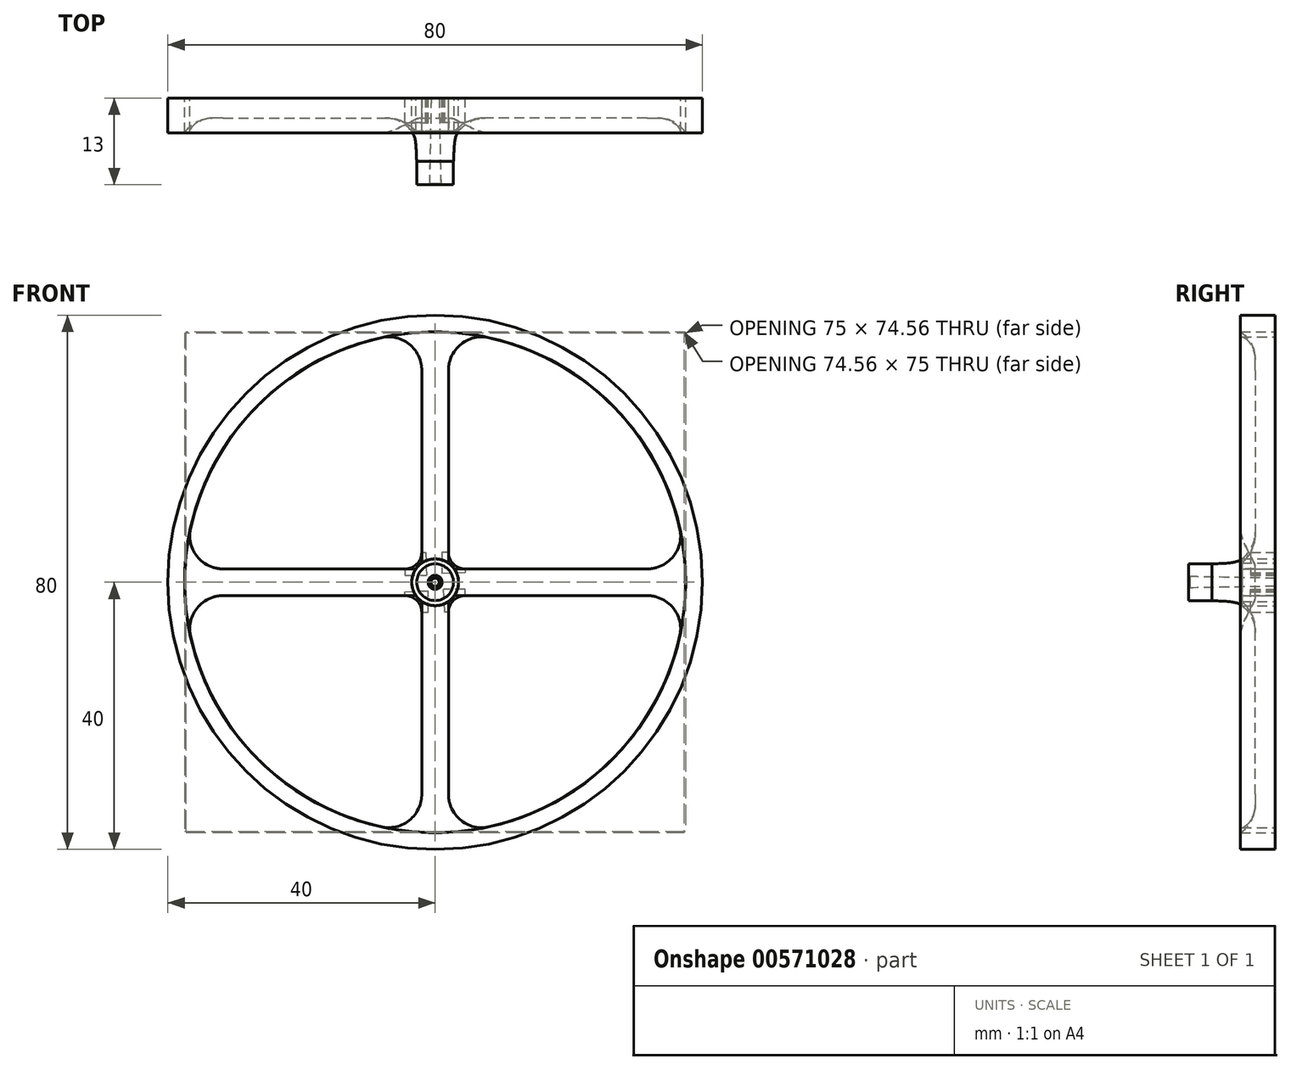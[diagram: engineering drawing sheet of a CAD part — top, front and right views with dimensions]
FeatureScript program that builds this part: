
annotation { "Feature Type Name" : "Feature", "Feature Type Description" : "" }
export const myFeature = defineFeature(function(context is Context, id is Id, definition is map)
    precondition{}
    {
        {
            var Q0;
            Q0=qCreatedBy(makeId("Front.planeOp"),FACE);
            var sketch = newSketch(context, id + "F0", { "sketchPlane" : qUnion([Q0])});
            skCircle(sketch, "E0", {"center": v(0, 0) * mm, "radius": 3.5 * mm});
            skSolve(sketch);
        }
        {
            var Q0;
            Q0=qSketchRegion(id+"F0",true);
            extrude(context, id + "F1", {"entities" : qUnion([Q0]), "depth" : 5 * mm});
        }
        {
            var Q0;
            Q0=qCreatedBy(makeId("Right.planeOp"),FACE);
            var sketch = newSketch(context, id + "F2", { "sketchPlane" : qUnion([Q0])});
            skLineSegment(sketch, "E1", {"start": v(3.77, 0) * mm, "end": v(-36.31, 0) * mm, "construction": true});
            skLineSegment(sketch, "E2", {"start": v(-13, 0) * mm, "end": v(-13, 2.75) * mm});
            skLineSegment(sketch, "E3", {"start": v(-13, 2.75) * mm, "end": v(-9.5, 2.75) * mm});
            skFitSpline(sketch, "E4", {"points": [v(-9.5, 2.75) * mm, v(-5, 3.5) * mm], "startDerivative": vector(5.34, 0.31) * mm, "endDerivative": vector(2.38, 2.14) * mm});
            skLineSegment(sketch, "E5", {"start": v(-5, 3.5) * mm, "end": v(-5, 0) * mm});
            skLineSegment(sketch, "E6", {"start": v(-5, 0) * mm, "end": v(-13, 0) * mm});
            skSolve(sketch);
        }
        {
            var Q0;
            Q0=qSketchRegion(id+"F2",true);
            var Q1;
            Q1=sQuery(id+"F2.wireOp",EDGE,"E1");
            revolve(context, id + "F3", {"operationType" : NewBodyOperationType.ADD, "entities" : qUnion([Q0]), "axis" : qUnion([Q1]), "revolveType" : RevolveType.FULL});
        }
        {
            var Q0;
            Q0=makeQuery(id+"F1.opExtrude","CAP_FACE",FACE,{"disambiguationData":[OSD([sQuery(id+"F0.wireOp",EDGE,"E0")])],"isStart":true});
            var sketch = newSketch(context, id + "F4", { "sketchPlane" : qUnion([Q0])});
            skCircle(sketch, "E7", {"center": v(0, 0) * mm, "radius": 0.6 * mm});
            skSolve(sketch);
        }
        {
            var Q0;
            Q0=qSketchRegion(id+"F4",true);
            extrude(context, id + "F5", {"entities" : qUnion([Q0]), "operationType" : NewBodyOperationType.REMOVE, "endBound" : BoundingType.THROUGH_ALL, "oppositeDirection" : true, "depth" : 25 * mm, "hasDraft" : true, "draftAngle" : 1.1 * degree});
        }
        {
            var Q0;
            Q0=qCreatedBy(makeId("Top.planeOp"),FACE);
            var sketch = newSketch(context, id + "F6", { "sketchPlane" : qUnion([Q0])});
            skLineSegment(sketch, "E8.bottom", {"start": v(-2, 0) * mm, "end": v(2, 0) * mm});
            skLineSegment(sketch, "E8.top", {"start": v(-2, -3) * mm, "end": v(2, -3) * mm});
            skLineSegment(sketch, "E8.left", {"start": v(-2, 0) * mm, "end": v(-2, -3) * mm});
            skLineSegment(sketch, "E8.right", {"start": v(2, 0) * mm, "end": v(2, -3) * mm});
            skSolve(sketch);
        }
        {
            var Q0;
            Q0=qSketchRegion(id+"F6",true);
            extrude(context, id + "F7", {"entities" : qUnion([Q0]), "operationType" : NewBodyOperationType.ADD, "depth" : 38 * mm, "hasSecondDirection" : true, "secondDirectionOppositeDirection" : false, "secondDirectionDepth" : 2.5 * mm, "offsetDistance" : 25 * mm});
        }
        {
            var Q0;
            Q0=makeQuery(id+"F5.boolean.opBoolean","INTERSECT",EDGE,{"derivedFrom":[makeQuery(id+"F3.opRevolve","SWEPT_FACE",FACE,{"disambiguationData":[OSD([sQuery(id+"F2.wireOp",EDGE,"E2")])]}),makeQuery(id+"F5.opExtrude","SWEPT_FACE",FACE,{"disambiguationData":[OSD([sQuery(id+"F4.wireOp",EDGE,"E7")])]})]});
            chamfer(context, id + "F8", {"entities" : qUnion([Q0]), "width" : .2 * mm, "tangentPropagation" : true});
        }
        {
            var Q0;
            Q0=makeQuery(id+"F7.boolean.opBoolean","MERGE",FACE,{"derivedFrom":[makeQuery(id+"F1.opExtrude","CAP_FACE",FACE,{"disambiguationData":[OSD([sQuery(id+"F0.wireOp",EDGE,"E0")])],"isStart":true}),makeQuery(id+"F7.opExtrude","SWEPT_FACE",FACE,{"disambiguationData":[OSD([sQuery(id+"F6.wireOp",EDGE,"E8.bottom")])]})]});
            var sketch = newSketch(context, id + "F9", { "sketchPlane" : qUnion([Q0])});
            skCircle(sketch, "E9", {"center": v(0, 0) * mm, "radius": 40 * mm});
            skCircle(sketch, "E10", {"center": v(0, 0) * mm, "radius": 37.5 * mm});
            skSolve(sketch);
        }
        {
            var Q0;
            Q0=qSketchRegion(id+"F9",true);
            extrude(context, id + "F10", {"entities" : qUnion([Q0]), "operationType" : NewBodyOperationType.ADD, "oppositeDirection" : true, "depth" : 5.2 * mm});
        }
        {
            var Q0;
            Q0=makeQuery(id+"F7.boolean.opBoolean","INTERSECT",EDGE,{"derivedFrom":[makeQuery(id+"F1.opExtrude","SWEPT_FACE",FACE,{"disambiguationData":[OSD([sQuery(id+"F0.wireOp",EDGE,"E0")])]}),makeQuery(id+"F7.opExtrude","SWEPT_FACE",FACE,{"disambiguationData":[OSD([sQuery(id+"F6.wireOp",EDGE,"E8.top")])]})]});
            var Q1;
            Q1=makeQuery(id+"F10.boolean.opBoolean","INTERSECT",EDGE,{"derivedFrom":[makeQuery(id+"F7.opExtrude","SWEPT_FACE",FACE,{"disambiguationData":[OSD([sQuery(id+"F6.wireOp",EDGE,"E8.top")])]}),makeQuery(id+"F10.opExtrude","SWEPT_FACE",FACE,{"disambiguationData":[OSD([sQuery(id+"F9.wireOp",EDGE,"E10")])]})]});
            fillet(context, id + "F11", {"entities" : qUnion([Q0, Q1]), "radius" : 5 * mm, "tangentPropagation" : true, "allowEdgeOverflow" : false});
        }
        {
            var Q0;
            Q0=makeQuery(id+"F10.boolean.opBoolean","INTERSECT",EDGE,{"derivedFrom":[makeQuery(id+"F7.opExtrude","SWEPT_FACE",FACE,{"disambiguationData":[OSD([sQuery(id+"F6.wireOp",EDGE,"E8.right")])]}),makeQuery(id+"F10.opExtrude","SWEPT_FACE",FACE,{"disambiguationData":[OSD([sQuery(id+"F9.wireOp",EDGE,"E10")])]})]});
            var Q1;
            Q1=makeQuery(id+"F10.boolean.opBoolean","INTERSECT",EDGE,{"derivedFrom":[makeQuery(id+"F7.opExtrude","SWEPT_FACE",FACE,{"disambiguationData":[OSD([sQuery(id+"F6.wireOp",EDGE,"E8.left")])]}),makeQuery(id+"F10.opExtrude","SWEPT_FACE",FACE,{"disambiguationData":[OSD([sQuery(id+"F9.wireOp",EDGE,"E10")])]})]});
            fillet(context, id + "F12", {"entities" : qUnion([Q0, Q1]), "radius" : 5 * mm, "tangentPropagation" : true, "allowEdgeOverflow" : false});
        }
        {
            var Q0;
            Q0=makeQuery(id+"F1.opExtrude","SWEPT_BODY",BODY,{"disambiguationData":[OSD([sQuery(id+"F0.wireOp",EDGE,"E0")])]});
            var Q1;
            Q1=makeQuery(id+"F3.opRevolve","SWEPT_FACE",FACE,{"disambiguationData":[OSD([sQuery(id+"F2.wireOp",EDGE,"E3")])]});
            circularPattern(context, id + "F13", {"entities" : qUnion([Q0]), "axis" : qUnion([Q1]), "angle" : 360 * degree, "instanceCount" : 4, "equalSpace" : true});
        }
        {
            var Q0;
            {var subQ0=makeQuery(id+"F10.boolean.opBoolean","MERGE",FACE,{"derivedFrom":[makeQuery(id+"F7.boolean.opBoolean","MERGE",FACE,{"derivedFrom":[makeQuery(id+"F1.opExtrude","CAP_FACE",FACE,{"disambiguationData":[OSD([sQuery(id+"F0.wireOp",EDGE,"E0")])],"isStart":true}),makeQuery(id+"F7.opExtrude","SWEPT_FACE",FACE,{"disambiguationData":[OSD([sQuery(id+"F6.wireOp",EDGE,"E8.bottom")])]})]}),makeQuery(id+"F10.opExtrude","CAP_FACE",FACE,{"disambiguationData":[OSD([sQuery(id+"F9.wireOp",EDGE,"E9"),sQuery(id+"F9.wireOp",EDGE,"E10")])],"isStart":true})]});Q0=makeQuery(id+"FgIhm2Tt6zTOsJ9_1.boolean.opBoolean","MERGE",FACE,{"derivedFrom":[makeQuery(id+"FDYBKFrb20v7z53_1.opBoolean","MERGE",FACE,{"derivedFrom":[subQ0,makeQuery(id+"F13.opPattern","COPY",FACE,{"derivedFrom":subQ0,"instanceName":"1"}),makeQuery(id+"F13.opPattern","COPY",FACE,{"derivedFrom":subQ0,"instanceName":"2"}),makeQuery(id+"F13.opPattern","COPY",FACE,{"derivedFrom":subQ0,"instanceName":"3"})]}),makeQuery(id+"FgIhm2Tt6zTOsJ9_1.opExtrude","CAP_FACE",FACE,{"disambiguationData":[OSD([sQuery(id+"FTYQuE2zEAQoyuF_1.wireOp",EDGE,"2QqTN2Jg-TwYb-xefx-Ns2m-0Et6M2J3xaq2"),sQuery(id+"FTYQuE2zEAQoyuF_1.wireOp",EDGE,"eRERD4EF-URZr-QwCf-6lY6-XNeSWXYZj7bk"),sQuery(id+"FTYQuE2zEAQoyuF_1.wireOp",EDGE,"w1udHuFG-gaxB-rpRy-TvAe-Q6hEAi3vOdkO"),sQuery(id+"FTYQuE2zEAQoyuF_1.wireOp",EDGE,"ccb8e607-9a5f-4511-8021-514936b70c73.filletArc"),sQuery(id+"FTYQuE2zEAQoyuF_1.wireOp",EDGE,"0a0adc1d-e557-4132-b897-d3ac198357fb.filletArc"),sQuery(id+"FTYQuE2zEAQoyuF_1.wireOp",EDGE,"b0aMqVTr-uXCx-4wKI-6uIc-G6YGe43DG1Aq"),sQuery(id+"FTYQuE2zEAQoyuF_1.wireOp",EDGE,"I1tABSEo-hI8d-lGJT-UJOT-oiTtTxIxys52"),sQuery(id+"FTYQuE2zEAQoyuF_1.wireOp",EDGE,"LAcF6vfi-sfcO-sjto-NgG3-pIlErQrigMXa"),sQuery(id+"FTYQuE2zEAQoyuF_1.wireOp",EDGE,"aqtcTmt6-T24C-q2HQ-cTpA-Y39zHsUlbNQ4")])],"isStart":true})]});}
            var sketch = newSketch(context, id + "F14", { "sketchPlane" : qUnion([Q0])});
            skArc(sketch, "E11", {"start": v(-4.5, 2) * mm, "mid": v(-2.73, 2.73) * mm, "end": v(-2, 4.5) * mm});
            skLineSegment(sketch, "E12", {"start": v(-2, 4.5) * mm, "end": v(-1.03, 4.5) * mm});
            skLineSegment(sketch, "E13", {"start": v(-1.03, 4.5) * mm, "end": v(-1.03, 1.28) * mm});
            skLineSegment(sketch, "E14", {"start": v(-4.5, 2) * mm, "end": v(-4.5, 1.43) * mm});
            skLineSegment(sketch, "E15", {"start": v(-4.5, 1.43) * mm, "end": v(-1.03, 1.28) * mm});
            skLineSegment(sketch, "E16.1.0", {"start": v(-4.5, -2) * mm, "end": v(-4.5, -1.03) * mm});
            skLineSegment(sketch, "E16.1.1", {"start": v(-4.5, -1.03) * mm, "end": v(-1.28, -1.03) * mm});
            skLineSegment(sketch, "E16.1.2", {"start": v(-1.43, -4.5) * mm, "end": v(-1.28, -1.03) * mm});
            skLineSegment(sketch, "E16.1.3", {"start": v(-2, -4.5) * mm, "end": v(-1.43, -4.5) * mm});
            skArc(sketch, "E16.1.4", {"start": v(-2, -4.5) * mm, "mid": v(-2.73, -2.73) * mm, "end": v(-4.5, -2) * mm});
            skLineSegment(sketch, "E16.2.0", {"start": v(2, -4.5) * mm, "end": v(1.03, -4.5) * mm});
            skLineSegment(sketch, "E16.2.1", {"start": v(1.03, -4.5) * mm, "end": v(1.03, -1.28) * mm});
            skLineSegment(sketch, "E16.2.2", {"start": v(4.5, -1.43) * mm, "end": v(1.03, -1.28) * mm});
            skLineSegment(sketch, "E16.2.3", {"start": v(4.5, -2) * mm, "end": v(4.5, -1.43) * mm});
            skArc(sketch, "E16.2.4", {"start": v(4.5, -2) * mm, "mid": v(2.73, -2.73) * mm, "end": v(2, -4.5) * mm});
            skLineSegment(sketch, "E16.3.0", {"start": v(4.5, 2) * mm, "end": v(4.5, 1.03) * mm});
            skLineSegment(sketch, "E16.3.1", {"start": v(4.5, 1.03) * mm, "end": v(1.28, 1.03) * mm});
            skLineSegment(sketch, "E16.3.2", {"start": v(1.43, 4.5) * mm, "end": v(1.28, 1.03) * mm});
            skLineSegment(sketch, "E16.3.3", {"start": v(2, 4.5) * mm, "end": v(1.43, 4.5) * mm});
            skArc(sketch, "E16.3.4", {"start": v(2, 4.5) * mm, "mid": v(2.73, 2.73) * mm, "end": v(4.5, 2) * mm});
            skPoint(sketch, "E16.center", {"position": v(0, 0) * mm});
            skSolve(sketch);
        }
        {
            var Q0;
            Q0=qSketchRegion(id+"F14",true);
            extrude(context, id + "F15", {"entities" : qUnion([Q0]), "oppositeDirection" : true, "depth" : 3.7 * mm});
        }
    });
